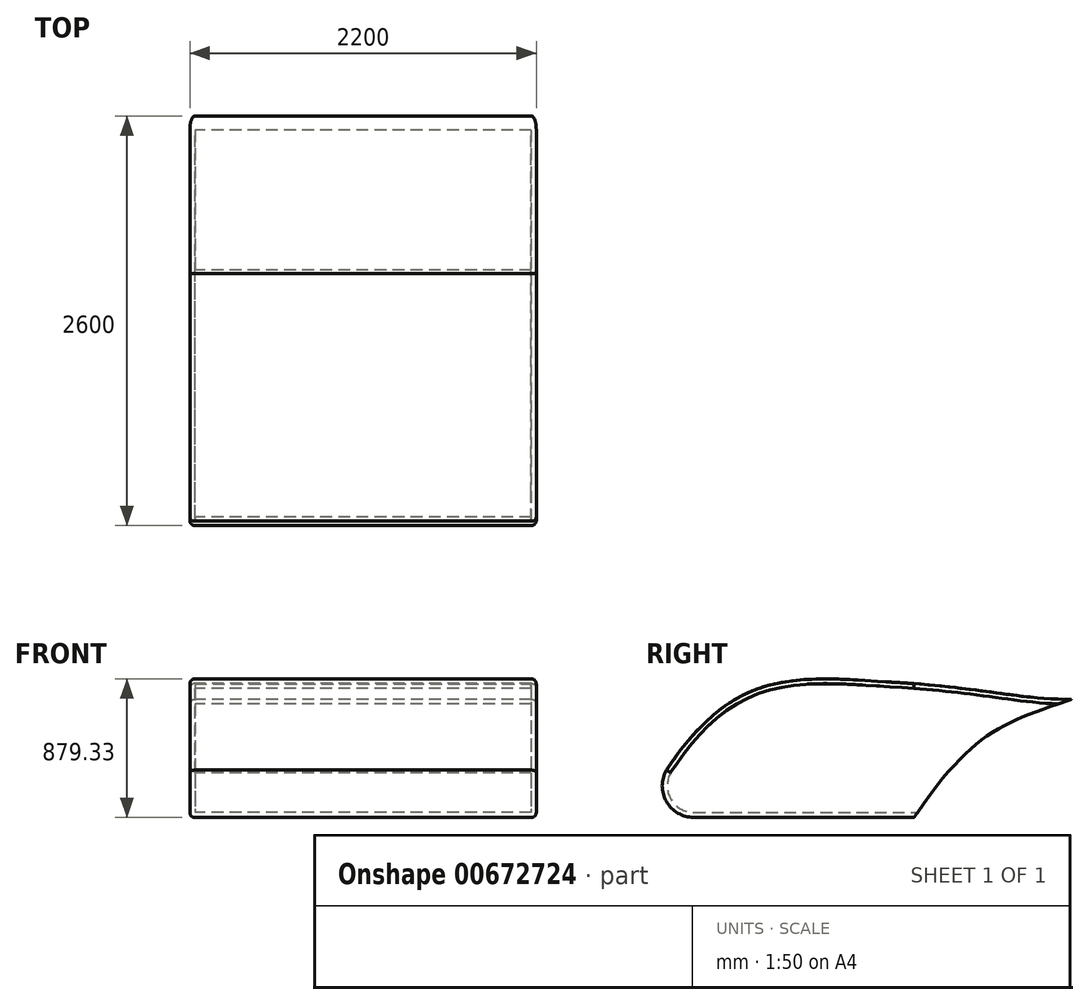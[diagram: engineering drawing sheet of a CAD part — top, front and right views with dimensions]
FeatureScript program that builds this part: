
annotation { "Feature Type Name" : "Feature", "Feature Type Description" : "" }
export const myFeature = defineFeature(function(context is Context, id is Id, definition is map)
    precondition{}
    {
        {
            var Q0;
            Q0=qCreatedBy(makeId("Right.planeOp"),FACE);
            var sketch = newSketch(context, id + "F0", { "sketchPlane" : qUnion([Q0])});
            skLineSegment(sketch, "E0", {"start": v(0, 0) * mm, "end": v(-1400, 0) * mm});
            skLineSegment(sketch, "E1", {"start": v(-1516.7, 0) * mm, "end": v(-1516.7, 0) * mm});
            skPoint(sketch, "E2.orphan", {"position": v(-1400, 0) * mm});
            skPoint(sketch, "E3.visualSharp", {"position": v(-1838.84, 0) * mm});
            skArc(sketch, "E3.filletArc", {"start": v(-1573.07, 300.24) * mm, "mid": v(-1573.27, 100.12) * mm, "end": v(-1400, 0) * mm});
            skPoint(sketch, "E4.visualSharp", {"position": v(-1100, 850) * mm});
            skLineSegment(sketch, "E5", {"start": v(0, 750) * mm, "end": v(1000, 750) * mm});
            skFitSpline(sketch, "E6", {"points": [v(1000, 750) * mm, v(0, 0) * mm], "startDerivative": vector(-1385.49, -474.37) * mm, "endDerivative": vector(-1106.12, -1622.41) * mm});
            skFitSpline(sketch, "E7", {"points": [v(0, 850) * mm, v(-1573.07, 300.24) * mm], "startDerivative": vector(-2153.17, 124.02) * mm, "endDerivative": vector(-1362.62, -2061.04) * mm});
            skFitSpline(sketch, "E8", {"points": [v(1000, 750) * mm, v(0, 850) * mm], "startDerivative": vector(-949.49, 0) * mm, "endDerivative": vector(-1641.78, 139.8) * mm});
            skSolve(sketch);
        }
        {
            var Q0;
            Q0=makeQuery(id+"F0.imprint","IMPRINT",FACE,{"disambiguationData":[TD([[makeQuery(id+"F0.imprint","IMPRINT",EDGE,{"derivedFrom":sQuery(id+"F0.wireOp",EDGE,"E0")}),-1.0]])]});
            extrude(context, id + "F1", {"entities" : qUnion([Q0]), "depth" : 2200 * mm, "offsetDistance" : 25 * mm});
        }
        {
            var Q0;
            Q0=makeQuery(id+"F1.opExtrude","CAP_EDGE",EDGE,{"disambiguationData":[OSD([sQuery(id+"F0.wireOp",EDGE,"E8")])],"isStart":true});
            var Q1;
            Q1=makeQuery(id+"F1.opExtrude","CAP_EDGE",EDGE,{"disambiguationData":[OSD([sQuery(id+"F0.wireOp",EDGE,"E7")])],"isStart":true});
            var Q2;
            Q2=makeQuery(id+"F1.opExtrude","CAP_EDGE",EDGE,{"disambiguationData":[OSD([sQuery(id+"F0.wireOp",EDGE,"E3.filletArc")])],"isStart":true});
            var Q3;
            Q3=makeQuery(id+"F1.opExtrude","CAP_EDGE",EDGE,{"disambiguationData":[OSD([sQuery(id+"F0.wireOp",EDGE,"E0")])],"isStart":false});
            var Q4;
            Q4=makeQuery(id+"F1.opExtrude","CAP_EDGE",EDGE,{"disambiguationData":[OSD([sQuery(id+"F0.wireOp",EDGE,"E7")])],"isStart":false});
            var Q5;
            Q5=makeQuery(id+"F1.opExtrude","CAP_EDGE",EDGE,{"disambiguationData":[OSD([sQuery(id+"F0.wireOp",EDGE,"E8")])],"isStart":false});
            fillet(context, id + "F2", {"entities" : qUnion([Q0, Q1, Q2, Q3, Q4, Q5]), "radius" : 30 * mm, "tangentPropagation" : true, "allowEdgeOverflow" : false});
        }
        {
            var Q0;
            Q0=makeQuery(id+"F1.opExtrude","SWEPT_FACE",FACE,{"disambiguationData":[OSD([sQuery(id+"F0.wireOp",EDGE,"E6")])]});
            shell(context, id + "F3", {"entities" : qUnion([Q0]), "thickness" : 32 * mm});
        }
    });
